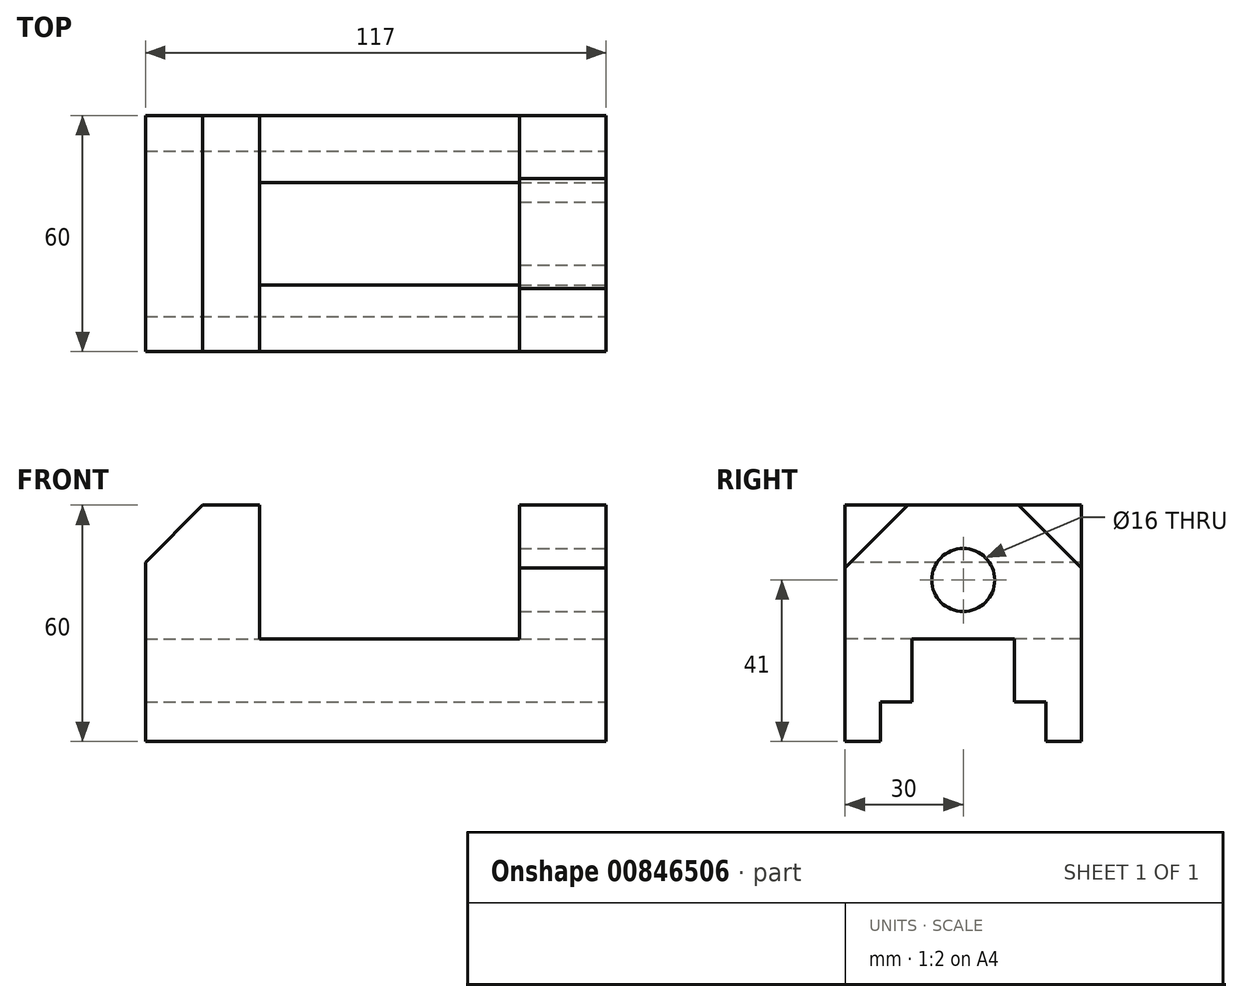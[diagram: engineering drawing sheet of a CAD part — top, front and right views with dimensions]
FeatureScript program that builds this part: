
annotation { "Feature Type Name" : "Feature", "Feature Type Description" : "" }
export const myFeature = defineFeature(function(context is Context, id is Id, definition is map)
    precondition{}
    {
        {
            var Q0;
            Q0=qCreatedBy(makeId("Front.planeOp"),FACE);
            var sketch = newSketch(context, id + "F0", { "sketchPlane" : qUnion([Q0])});
            skLineSegment(sketch, "E0.bottom", {"start": v(0, 0) * mm, "end": v(117, 0) * mm});
            skLineSegment(sketch, "E0.top", {"start": v(0, 60) * mm, "end": v(117, 60) * mm});
            skLineSegment(sketch, "E0.left", {"start": v(0, 0) * mm, "end": v(0, 60) * mm});
            skLineSegment(sketch, "E0.right", {"start": v(117, 0) * mm, "end": v(117, 60) * mm});
            skSolve(sketch);
        }
        {
            var Q0;
            Q0 = qSketchRegion(id + "F0", true);
            extrude(context, id + "F1", {"entities" : qUnion([Q0]), "depth" : 60 * mm, "offsetDistance" : 25.4 * mm});
        }
        {
            var Q0;
            Q0=makeQuery(id+"F1.opExtrude","CAP_FACE",FACE,{"disambiguationData":[OSD([sQuery(id+"F0.wireOp",EDGE,"E0.bottom"),sQuery(id+"F0.wireOp",EDGE,"E0.top"),sQuery(id+"F0.wireOp",EDGE,"E0.left"),sQuery(id+"F0.wireOp",EDGE,"E0.right")])],"isStart":false});
            var sketch = newSketch(context, id + "F2", { "sketchPlane" : qUnion([Q0])});
            skLineSegment(sketch, "E1", {"start": v(0, 60) * mm, "end": v(29, 60) * mm});
            skLineSegment(sketch, "E2", {"start": v(29, 60) * mm, "end": v(29, 26) * mm});
            skLineSegment(sketch, "E3", {"start": v(29, 26) * mm, "end": v(95, 26) * mm});
            skLineSegment(sketch, "E4", {"start": v(95, 26) * mm, "end": v(95, 60) * mm});
            skLineSegment(sketch, "E5", {"start": v(95, 60) * mm, "end": v(117, 60) * mm});
            skSolve(sketch);
        }
        {
            var Q0;
            {var subQ0=sQuery(id+"F2.wireOp",EDGE,"E2");Q0=makeQuery(id+"F2.imprint","IMPRINT",FACE,{"disambiguationData":[TD([[makeQuery(id+"F2.imprint","IMPRINT",EDGE,{"derivedFrom":subQ0}),1.0]])]});}
            extrude(context, id + "F3", {"entities" : qUnion([Q0]), "operationType" : NewBodyOperationType.REMOVE, "endBound" : BoundingType.THROUGH_ALL, "oppositeDirection" : true, "depth" : 25.4 * mm, "offsetDistance" : 25.4 * mm});
        }
        {
            var Q0;
            Q0=makeQuery(id+"F1.opExtrude","CAP_FACE",FACE,{"disambiguationData":[OSD([sQuery(id+"F0.wireOp",EDGE,"E0.bottom"),sQuery(id+"F0.wireOp",EDGE,"E0.top"),sQuery(id+"F0.wireOp",EDGE,"E0.left"),sQuery(id+"F0.wireOp",EDGE,"E0.right")])],"isStart":false});
            var sketch = newSketch(context, id + "F4", { "sketchPlane" : qUnion([Q0])});
            skLineSegment(sketch, "E6", {"start": v(29, 60) * mm, "end": v(14.5, 60) * mm});
            skLineSegment(sketch, "E7", {"start": v(14.5, 60) * mm, "end": v(0, 45.5) * mm});
            skLineSegment(sketch, "E8", {"start": v(0, 45.5) * mm, "end": v(0, 60) * mm});
            skLineSegment(sketch, "E9", {"start": v(0, 60) * mm, "end": v(14.5, 60) * mm});
            skSolve(sketch);
        }
        {
            var Q0;
            Q0 = qSketchRegion(id + "F4", true);
            extrude(context, id + "F5", {"entities" : qUnion([Q0]), "operationType" : NewBodyOperationType.REMOVE, "endBound" : BoundingType.THROUGH_ALL, "oppositeDirection" : true, "depth" : 25.4 * mm, "offsetDistance" : 25.4 * mm});
        }
        {
            var Q0;
            Q0=makeQuery(id+"F1.opExtrude","SWEPT_FACE",FACE,{"disambiguationData":[OSD([sQuery(id+"F0.wireOp",EDGE,"E0.right")])]});
            var sketch = newSketch(context, id + "F6", { "sketchPlane" : qUnion([Q0])});
            skLineSegment(sketch, "E10", {"start": v(-60, 0) * mm, "end": v(-51, 0) * mm});
            skLineSegment(sketch, "E11", {"start": v(-51, 0) * mm, "end": v(-51, 10) * mm});
            skLineSegment(sketch, "E12", {"start": v(-51, 10) * mm, "end": v(-43, 10) * mm});
            skLineSegment(sketch, "E13", {"start": v(-43, 10) * mm, "end": v(-43, 26) * mm});
            skLineSegment(sketch, "E14", {"start": v(-43, 26) * mm, "end": v(-17, 26) * mm});
            skLineSegment(sketch, "E15", {"start": v(-17, 26) * mm, "end": v(-17, 10) * mm});
            skLineSegment(sketch, "E16", {"start": v(-17, 10) * mm, "end": v(-9, 10) * mm});
            skLineSegment(sketch, "E17", {"start": v(-9, 10) * mm, "end": v(-9, 0) * mm});
            skLineSegment(sketch, "E18", {"start": v(-9, 0) * mm, "end": v(0, 0) * mm});
            skSolve(sketch);
        }
        {
            var Q0;
            {var subQ0=sQuery(id+"F6.wireOp",EDGE,"E11");Q0=makeQuery(id+"F6.imprint","IMPRINT",FACE,{"disambiguationData":[TD([[makeQuery(id+"F6.imprint","IMPRINT",EDGE,{"derivedFrom":subQ0}),-1.0]])]});}
            extrude(context, id + "F7", {"entities" : qUnion([Q0]), "operationType" : NewBodyOperationType.REMOVE, "endBound" : BoundingType.THROUGH_ALL, "oppositeDirection" : true, "depth" : 25.4 * mm, "offsetDistance" : 25.4 * mm});
        }
        {
            var Q0;
            Q0=makeQuery(id+"F1.opExtrude","SWEPT_FACE",FACE,{"disambiguationData":[OSD([sQuery(id+"F0.wireOp",EDGE,"E0.right")])]});
            var sketch = newSketch(context, id + "F8", { "sketchPlane" : qUnion([Q0])});
            skLineSegment(sketch, "E19", {"start": v(-60, 60) * mm, "end": v(-44, 60) * mm});
            skLineSegment(sketch, "E20", {"start": v(-44, 60) * mm, "end": v(-60, 44) * mm});
            skLineSegment(sketch, "E21", {"start": v(-60, 44) * mm, "end": v(-60, 60) * mm});
            skLineSegment(sketch, "E22", {"start": v(0, 60) * mm, "end": v(-16, 60) * mm});
            skLineSegment(sketch, "E23", {"start": v(-16, 60) * mm, "end": v(0, 44) * mm});
            skLineSegment(sketch, "E24", {"start": v(0, 44) * mm, "end": v(0, 60) * mm});
            skSolve(sketch);
        }
        {
            var Q0;
            Q0=makeQuery(id+"F8.imprint","IMPRINT",FACE,{"disambiguationData":[TD([[makeQuery(id+"F8.imprint","IMPRINT",EDGE,{"derivedFrom":sQuery(id+"F8.wireOp",EDGE,"E19")}),-1.0]])]});
            var Q1;
            Q1=makeQuery(id+"F8.imprint","IMPRINT",FACE,{"disambiguationData":[TD([[makeQuery(id+"F8.imprint","IMPRINT",EDGE,{"derivedFrom":sQuery(id+"F8.wireOp",EDGE,"E22")}),-1.0]])]});
            extrude(context, id + "F9", {"entities" : qUnion([Q0, Q1]), "operationType" : NewBodyOperationType.REMOVE, "oppositeDirection" : true, "depth" : 22 * mm, "offsetDistance" : 25.4 * mm});
        }
        {
            var Q0;
            Q0=makeQuery(id+"F1.opExtrude","SWEPT_FACE",FACE,{"disambiguationData":[OSD([sQuery(id+"F0.wireOp",EDGE,"E0.right")])]});
            var sketch = newSketch(context, id + "F10", { "sketchPlane" : qUnion([Q0])});
            skCircle(sketch, "E25", {"center": v(-30, 41) * mm, "radius": 8 * mm});
            skSolve(sketch);
        }
        {
            var Q0;
            Q0 = qSketchRegion(id + "F10", true);
            extrude(context, id + "F11", {"entities" : qUnion([Q0]), "operationType" : NewBodyOperationType.REMOVE, "oppositeDirection" : true, "depth" : 22 * mm, "offsetDistance" : 25.4 * mm});
        }
    });
